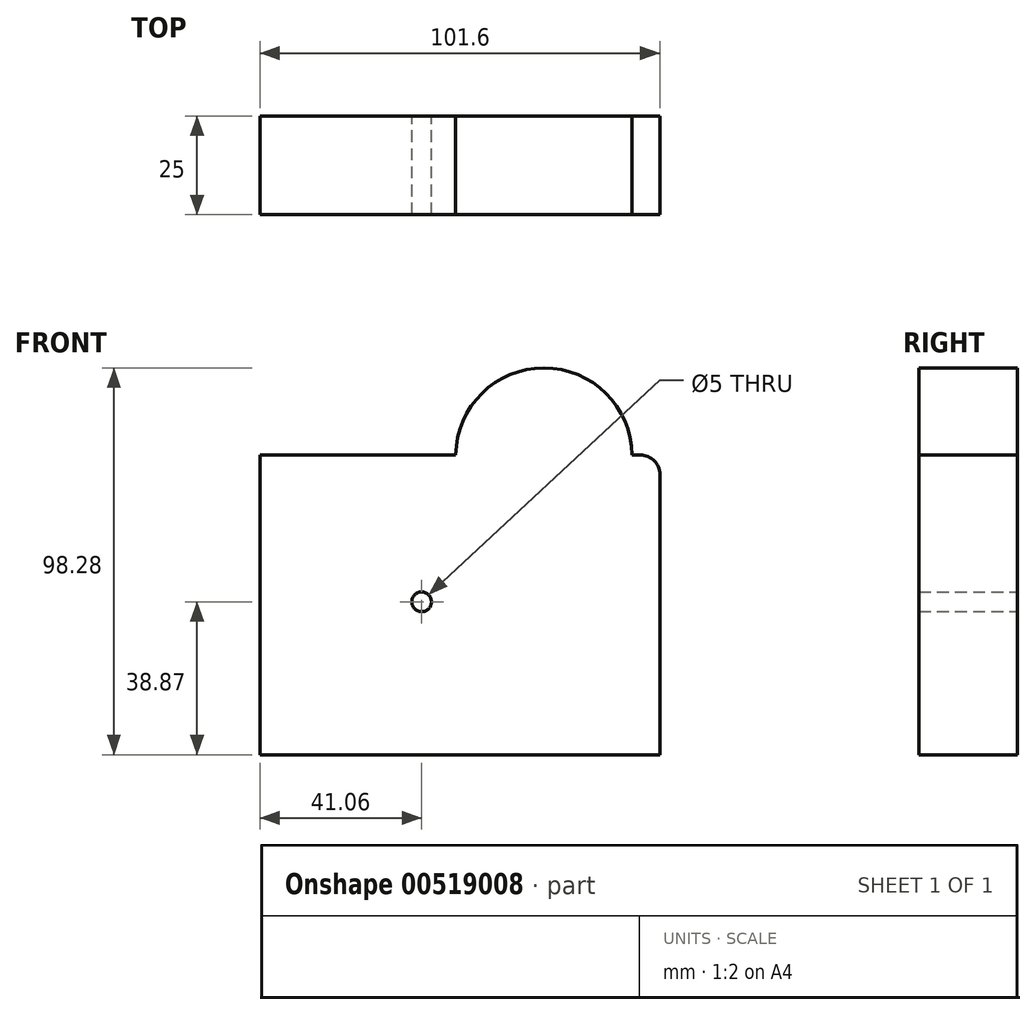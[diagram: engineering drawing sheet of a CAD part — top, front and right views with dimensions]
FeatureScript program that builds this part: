
annotation { "Feature Type Name" : "Feature", "Feature Type Description" : "" }
export const myFeature = defineFeature(function(context is Context, id is Id, definition is map)
    precondition{}
    {
        {
            var Q0;
            Q0=qCreatedBy(makeId("Front.planeOp"),FACE);
            var sketch = newSketch(context, id + "F0", { "sketchPlane" : qUnion([Q0])});
            skLineSegment(sketch, "E0.bottom", {"start": v(-41.06, 37.33) * mm, "end": v(60.54, 37.33) * mm});
            skLineSegment(sketch, "E0.top", {"start": v(-41.06, -38.87) * mm, "end": v(60.54, -38.87) * mm});
            skLineSegment(sketch, "E0.left", {"start": v(-41.06, 37.33) * mm, "end": v(-41.06, -38.87) * mm});
            skLineSegment(sketch, "E0.right", {"start": v(60.54, 37.33) * mm, "end": v(60.54, -38.87) * mm});
            skSolve(sketch);
        }
        {
            var Q0;
            Q0=makeQuery(id+"F0.imprint","IMPRINT",FACE,{"disambiguationData":[TD([[makeQuery(id+"F0.imprint","IMPRINT",EDGE,{"derivedFrom":sQuery(id+"F0.wireOp",EDGE,"E0.bottom")}),-1.0]])]});
            extrude(context, id + "F1", {"entities" : qUnion([Q0]), "depth" : 25 * mm, "offsetDistance" : 25 * mm});
        }
        {
            var Q0;
            Q0=makeQuery(id+"F1.opExtrude","SWEPT_EDGE",EDGE,{"disambiguationData":[OSD([sQuery(id+"F0.wireOp",EDGE,"E0.bottom"),sQuery(id+"F0.wireOp",EDGE,"E0.right")])]});
            fillet(context, id + "F2", {"entities" : qUnion([Q0]), "radius" : 5 * mm, "tangentPropagation" : true, "allowEdgeOverflow" : false});
        }
        {
            var Q0;
            Q0=makeQuery(id+"F1.opExtrude","CAP_FACE",FACE,{"disambiguationData":[OSD([sQuery(id+"F0.wireOp",EDGE,"E0.bottom"),sQuery(id+"F0.wireOp",EDGE,"E0.top"),sQuery(id+"F0.wireOp",EDGE,"E0.left"),sQuery(id+"F0.wireOp",EDGE,"E0.right")])],"isStart":true});
            var sketch = newSketch(context, id + "F3", { "sketchPlane" : qUnion([Q0])});
            skCircle(sketch, "E1", {"center": v(0, 0) * mm, "radius": 28.3 * mm});
            skSolve(sketch);
        }
        {
            var Q0;
            Q0=sQuery(id+"F3.wireOp",VERTEX,"E1.center");
            var Q1;
            Q1=makeQuery(id+"F1.opExtrude","SWEPT_BODY",BODY,{"disambiguationData":[OSD([sQuery(id+"F0.wireOp",EDGE,"E0.bottom"),sQuery(id+"F0.wireOp",EDGE,"E0.top"),sQuery(id+"F0.wireOp",EDGE,"E0.left"),sQuery(id+"F0.wireOp",EDGE,"E0.right")])]});
            hole(context, id + "F4", {"style" : HoleStyle.SIMPLE, "endStyle" : HoleEndStyle.THROUGH, "holeDiameter" : 5 * mm, "isTappedThrough" : true, "tappedDepth" : 12 * mm, "tapClearance" : 3, "locations" : qUnion([Q0]), "scope" : qUnion([Q1])});
        }
        {
            var Q0;
            Q0=qCreatedBy(makeId("Front.planeOp"),FACE);
            var sketch = newSketch(context, id + "F5", { "sketchPlane" : qUnion([Q0])});
            skCircle(sketch, "E2", {"center": v(31.06, 37.01) * mm, "radius": 22.4 * mm});
            skSolve(sketch);
        }
        {
            var Q0;
            Q0=makeQuery(id+"F5.imprint","IMPRINT",FACE,{"disambiguationData":[TD([[makeQuery(id+"F5.imprint","IMPRINT",EDGE,{"derivedFrom":sQuery(id+"F5.wireOp",EDGE,"E2")}),1.0]])]});
            extrude(context, id + "F6", {"entities" : qUnion([Q0]), "operationType" : NewBodyOperationType.ADD, "depth" : 25 * mm, "offsetDistance" : 25 * mm});
        }
    });
